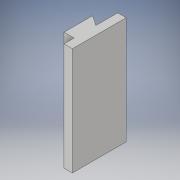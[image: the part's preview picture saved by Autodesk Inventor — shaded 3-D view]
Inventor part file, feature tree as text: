
AUTODESK INVENTOR PART (.ipt)
format: ipt  version: 2019 (Build 230136000, 136)  size: 98,816 bytes
history: native  units: mm
features: extrude x1, sketch x1
ambient origin geometry x8: Origin, YZ Plane, XZ Plane, XY Plane, X Axis, Y Axis, Z Axis, Center Point
bodies: Solid1 (feature_tree)
feature tree (2):
  extrude  "Extrusion1"  Depth=16.0mm
  sketch  "Sketch2"  dims[d1=2.5mm d2=16.0mm d3=3.0mm d4=6.5mm d5=3.0mm d6=8.5mm d7=32.0mm d8=0.0mm]
